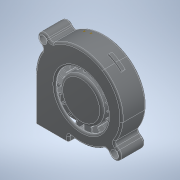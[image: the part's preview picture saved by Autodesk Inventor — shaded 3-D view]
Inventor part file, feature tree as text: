
AUTODESK INVENTOR PART (.ipt)
format: ipt  version: 2022 (Build 260153000, 153)  size: 379,904 bytes
history: imported  units: in
note: dims shown in document units (in); Inventor stores cm internally (conversion verified against a paired STEP export)
features: imported_body x1
ambient origin geometry x8: Origin, YZ Plane, XZ Plane, XY Plane, X Axis, Y Axis, Z Axis, Center Point
bodies: Solid1 (imported_parasolid), Body1 (imported_parasolid)
feature tree (1):
  imported_body  NMx_Import_Brep_tag  [imported B-rep: ~220 faces, bbox_mm=[52.8, 51.019694, 15.0]]
